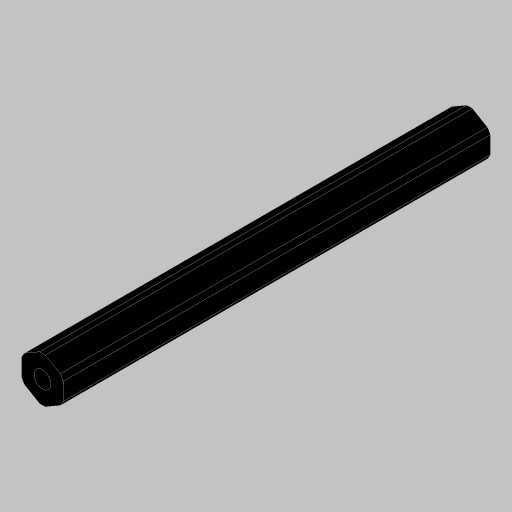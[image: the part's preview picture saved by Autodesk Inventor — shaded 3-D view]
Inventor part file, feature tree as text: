
AUTODESK INVENTOR PART (.ipt)
format: ipt  version: 2023.5 (Build 275446000, 446)  size: 195,072 bytes
history: native  units: in
note: dims shown in document units (in); Inventor stores cm internally (conversion verified against a paired STEP export)
features: extrude x2, projected_geometry x2, hole x1
ambient origin geometry x8: Origin, YZ Plane, XZ Plane, XY Plane, X Axis, Y Axis, Z Axis, Center Point
bodies: Solid1 (feature_tree)
feature tree (5):
  extrude  "Extrusion1"  TaperAngle=0.0deg  [1 undecoded]
  hole  "Hole1"  [1 undecoded]
  extrude  "Extrusion3"  TaperAngle=0.0deg  [1 undecoded]
  projected_geometry  "Project Cut Edges1"
  projected_geometry  "Project Cut Edges2"
note: 3 required parameter values undecoded (feature->parameter linkage not recoverable at this tier; creation-order binding heuristic only, values carry confidence <= 0.55)
